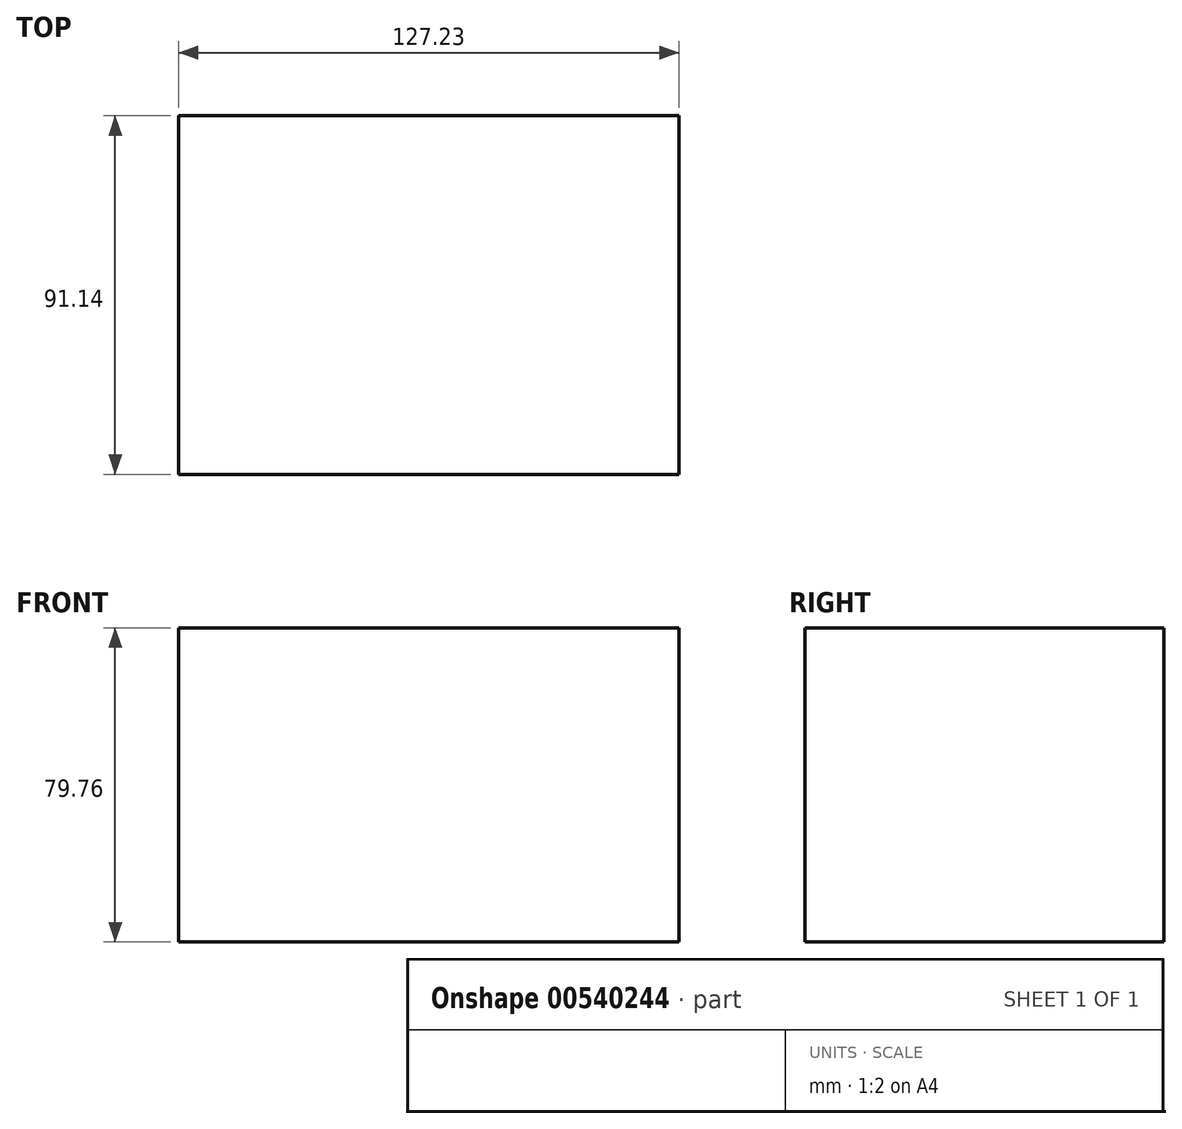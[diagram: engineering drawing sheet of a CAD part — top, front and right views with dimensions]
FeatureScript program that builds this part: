
annotation { "Feature Type Name" : "Feature", "Feature Type Description" : "" }
export const myFeature = defineFeature(function(context is Context, id is Id, definition is map)
    precondition{}
    {
        {
            var Q0;
            Q0=qCreatedBy(makeId("Top.planeOp"),FACE);
            var sketch = newSketch(context, id + "F0", { "sketchPlane" : qUnion([Q0])});
            skLineSegment(sketch, "E0.bottom", {"start": v(-65.27, 52.34) * mm, "end": v(61.96, 52.34) * mm});
            skLineSegment(sketch, "E0.top", {"start": v(-65.27, -38.8) * mm, "end": v(61.96, -38.8) * mm});
            skLineSegment(sketch, "E0.left", {"start": v(-65.27, 52.34) * mm, "end": v(-65.27, -38.8) * mm});
            skLineSegment(sketch, "E0.right", {"start": v(61.96, 52.34) * mm, "end": v(61.96, -38.8) * mm});
            skSolve(sketch);
        }
        {
            var Q0;
            Q0=makeQuery(id+"F0.imprint","IMPRINT",FACE,{"disambiguationData":[TD([[makeQuery(id+"F0.imprint","IMPRINT",EDGE,{"derivedFrom":sQuery(id+"F0.wireOp",EDGE,"E0.bottom")}),-1.0]])]});
            extrude(context, id + "F1", {"entities" : qUnion([Q0]), "depth" : 79.76 * mm, "offsetDistance" : 25.4 * mm});
        }
    });
